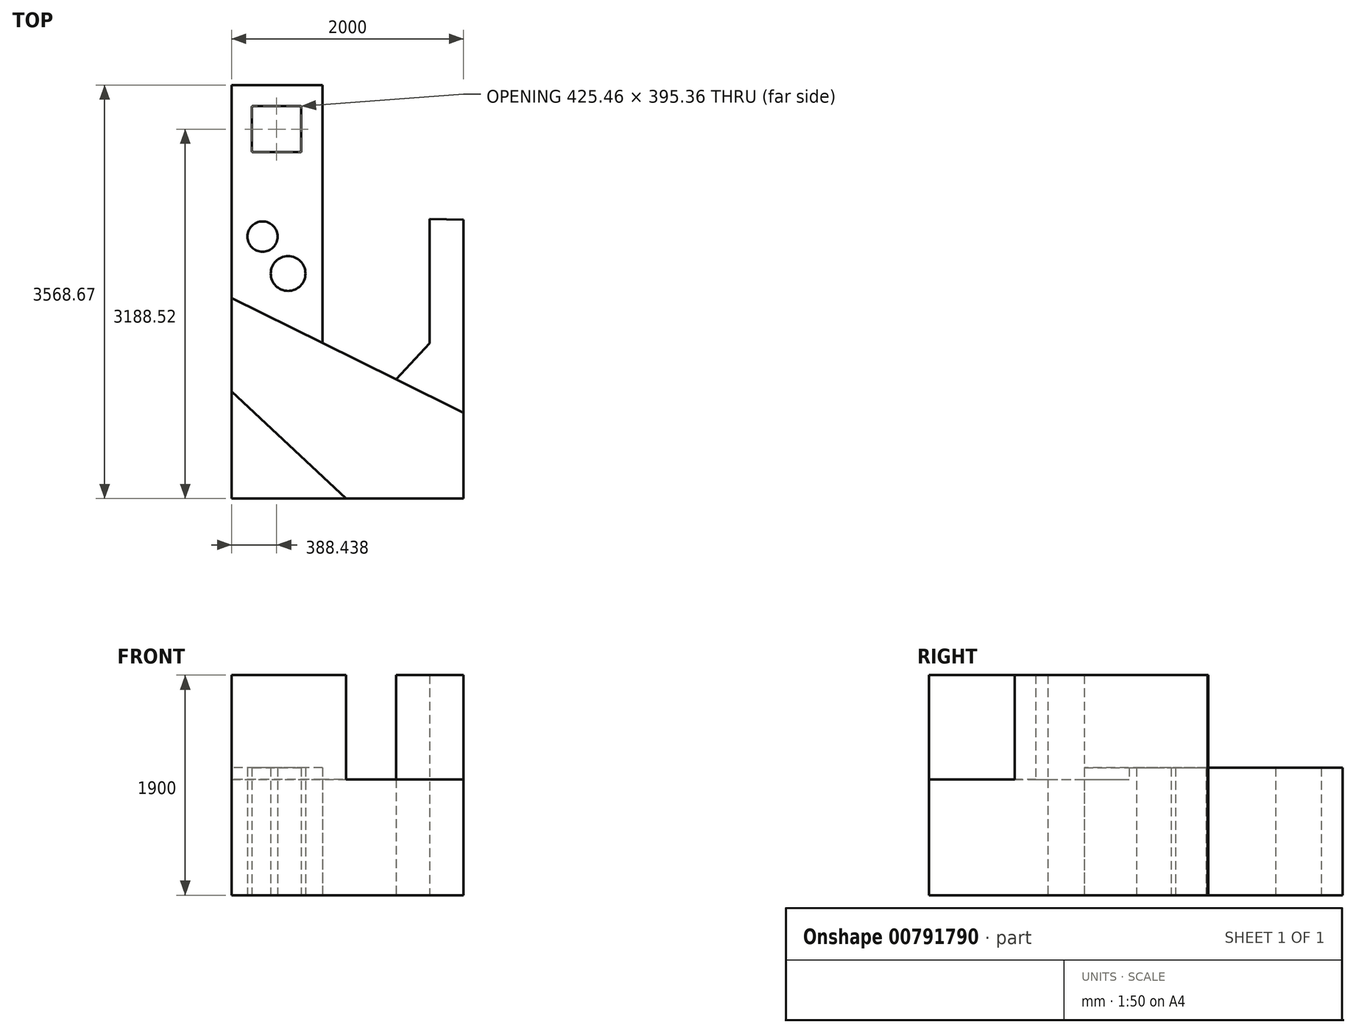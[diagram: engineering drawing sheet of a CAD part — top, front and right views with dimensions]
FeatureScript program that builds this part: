
annotation { "Feature Type Name" : "Feature", "Feature Type Description" : "" }
export const myFeature = defineFeature(function(context is Context, id is Id, definition is map)
    precondition{}
    {
        {
            var Q0;
            Q0=qCreatedBy(makeId("Top.planeOp"),FACE);
            var sketch = newSketch(context, id + "F0", { "sketchPlane" : qUnion([Q0])});
            skLineSegment(sketch, "E0.bottom", {"start": v(2000, 0) * mm, "end": v(0, 0) * mm});
            skLineSegment(sketch, "E0.top", {"start": v(2000, 4000) * mm, "end": v(0, 4000) * mm});
            skLineSegment(sketch, "E0.left", {"start": v(2000, 0) * mm, "end": v(2000, 4000) * mm});
            skLineSegment(sketch, "E0.right", {"start": v(0, 0) * mm, "end": v(0, 4000) * mm});
            skPoint(sketch, "E1", {"position": v(1534.17, 0) * mm});
            skLineSegment(sketch, "E2.top", {"start": v(0, 3568.67) * mm, "end": v(783.5, 3568.67) * mm});
            skLineSegment(sketch, "E2.left", {"start": v(0, 1728.74) * mm, "end": v(0, 3568.67) * mm});
            skLineSegment(sketch, "E2.right", {"start": v(783.5, 1728.74) * mm, "end": v(783.5, 3568.67) * mm});
            skLineSegment(sketch, "E3.bottom", {"start": v(2000, 4000) * mm, "end": v(2439.74, 4000) * mm});
            skLineSegment(sketch, "E3.top", {"start": v(2000, 2405.41) * mm, "end": v(2439.74, 2405.41) * mm});
            skLineSegment(sketch, "E3.left", {"start": v(2000, 4000) * mm, "end": v(2000, 2405.41) * mm});
            skLineSegment(sketch, "E3.right", {"start": v(2439.74, 4000) * mm, "end": v(2439.74, 2405.41) * mm});
            skLineSegment(sketch, "E4", {"start": v(1417.56, 1028.19) * mm, "end": v(2000, 1652.71) * mm});
            skLineSegment(sketch, "E5", {"start": v(1708.78, 1340.45) * mm, "end": v(1708.78, 2412.76) * mm});
            skLineSegment(sketch, "E6", {"start": v(1708.78, 2412.76) * mm, "end": v(2000, 2405.41) * mm});
            skLineSegment(sketch, "E7", {"start": v(0, 922.82) * mm, "end": v(1000, -11.87) * mm});
            skPoint(sketch, "E7.endSnap0", {"position": v(1000, 0) * mm});
            skLineSegment(sketch, "E8", {"start": v(2000, 740.35) * mm, "end": v(0, 1728.74) * mm});
            skLineSegment(sketch, "E9", {"start": v(0, 1257.36) * mm, "end": v(2000, 0) * mm, "construction": true});
            skLineSegment(sketch, "E10", {"start": v(1353.31, 0) * mm, "end": v(0, 1257.36) * mm, "construction": true});
            skLineSegment(sketch, "E11", {"start": v(2000, 466.64) * mm, "end": v(0, 1455.03) * mm, "construction": true});
            skLineSegment(sketch, "E12", {"start": v(783.5, 1728.74) * mm, "end": v(783.5, 1341.54) * mm});
            skCircle(sketch, "E13", {"center": v(266.88, 2260.95) * mm, "radius": 130.77 * mm});
            skCircle(sketch, "E14", {"center": v(487.2, 1941.63) * mm, "radius": 149.74 * mm});
            skLineSegment(sketch, "E15.bottom", {"start": v(180.71, 3386.2) * mm, "end": v(596.17, 3386.2) * mm});
            skLineSegment(sketch, "E15.top", {"start": v(180.71, 2990.84) * mm, "end": v(596.17, 2990.84) * mm});
            skLineSegment(sketch, "E15.left", {"start": v(175.71, 3381.2) * mm, "end": v(175.71, 2995.84) * mm});
            skLineSegment(sketch, "E15.right", {"start": v(601.17, 3381.2) * mm, "end": v(601.17, 2995.84) * mm});
            skPoint(sketch, "E16.visualSharp", {"position": v(175.71, 3386.2) * mm});
            skArc(sketch, "E16.filletArc", {"start": v(180.71, 3386.2) * mm, "mid": v(177.17, 3384.74) * mm, "end": v(175.71, 3381.2) * mm});
            skPoint(sketch, "E17.visualSharp", {"position": v(601.17, 3386.2) * mm});
            skArc(sketch, "E17.filletArc", {"start": v(601.17, 3381.2) * mm, "mid": v(599.7, 3384.74) * mm, "end": v(596.17, 3386.2) * mm});
            skPoint(sketch, "E18.visualSharp", {"position": v(601.17, 2990.84) * mm});
            skArc(sketch, "E18.filletArc", {"start": v(596.17, 2990.84) * mm, "mid": v(599.7, 2992.3) * mm, "end": v(601.17, 2995.84) * mm});
            skPoint(sketch, "E19.visualSharp", {"position": v(175.71, 2990.84) * mm});
            skArc(sketch, "E19.filletArc", {"start": v(175.71, 2995.84) * mm, "mid": v(177.17, 2992.3) * mm, "end": v(180.71, 2990.84) * mm});
            skSolve(sketch);
        }
        {
            var Q0;
            {var subQ0=sQuery(id+"F0.wireOp",EDGE,"E0.right");var subQ1=sQuery(id+"F0.wireOp",EDGE,"E0.bottom");var subQ2=makeQuery(id+"F0.imprint","INTERSECT",VERTEX,{"derivedFrom":[subQ1,subQ0]});Q0=makeQuery(id+"F0.imprint","IMPRINT",FACE,{"disambiguationData":[TD([[makeQuery(id+"F0.imprint","IMPRINT",EDGE,{"disambiguationData":[TD([[subQ2,1.0]])],"derivedFrom":subQ1}),-1.0]])]});}
            extrude(context, id + "F1", {"entities" : qUnion([Q0]), "depth" : 1900 * mm, "offsetDistance" : 25 * mm});
        }
        {
            var Q0;
            {var subQ5=sQuery(id+"F0.wireOp",EDGE,"E0.left");var subQ6=sQuery(id+"F0.wireOp",EDGE,"E0.bottom");var subQ7=makeQuery(id+"F0.imprint","INTERSECT",VERTEX,{"derivedFrom":[subQ6,subQ5]});Q0=makeQuery(id+"F0.imprint","IMPRINT",FACE,{"disambiguationData":[TD([[makeQuery(id+"F0.imprint","IMPRINT",EDGE,{"disambiguationData":[TD([[subQ7,-1.0]])],"derivedFrom":subQ6}),-1.0]])]});}
            extrude(context, id + "F2", {"entities" : qUnion([Q0]), "operationType" : NewBodyOperationType.ADD, "depth" : 1000 * mm, "offsetDistance" : 25 * mm});
        }
        {
            var Q0;
            Q0=makeQuery(id+"F0.imprint","IMPRINT",FACE,{"disambiguationData":[TD([[makeQuery(id+"F0.imprint","IMPRINT",EDGE,{"derivedFrom":sQuery(id+"F0.wireOp",EDGE,"E2.top")}),-1.0]])]});
            extrude(context, id + "F3", {"entities" : qUnion([Q0]), "operationType" : NewBodyOperationType.ADD, "depth" : 1100 * mm, "offsetDistance" : 25 * mm});
        }
        {
            var Q0;
            {var subQ0=sQuery(id+"F0.wireOp",EDGE,"E4");var subQ1=sQuery(id+"F0.wireOp",EDGE,"E0.left");var subQ2=makeQuery(id+"F0.imprint","INTERSECT",VERTEX,{"derivedFrom":[subQ1,subQ0]});Q0=makeQuery(id+"F0.imprint","IMPRINT",FACE,{"disambiguationData":[TD([[makeQuery(id+"F0.imprint","IMPRINT",EDGE,{"disambiguationData":[TD([[subQ2,1.0]])],"derivedFrom":subQ1}),1.0]])]});}
            extrude(context, id + "F4", {"entities" : qUnion([Q0]), "operationType" : NewBodyOperationType.ADD, "depth" : 1900 * mm, "offsetDistance" : 25 * mm});
        }
        {
            var Q0;
            {var subQ4=sQuery(id+"F0.wireOp",EDGE,"E5");Q0=makeQuery(id+"F0.imprint","IMPRINT",FACE,{"disambiguationData":[TD([[makeQuery(id+"F0.imprint","IMPRINT",EDGE,{"derivedFrom":subQ4}),-1.0]])]});}
            extrude(context, id + "F5", {"entities" : qUnion([Q0]), "operationType" : NewBodyOperationType.ADD, "depth" : 1900 * mm, "offsetDistance" : 25 * mm});
        }
    });
